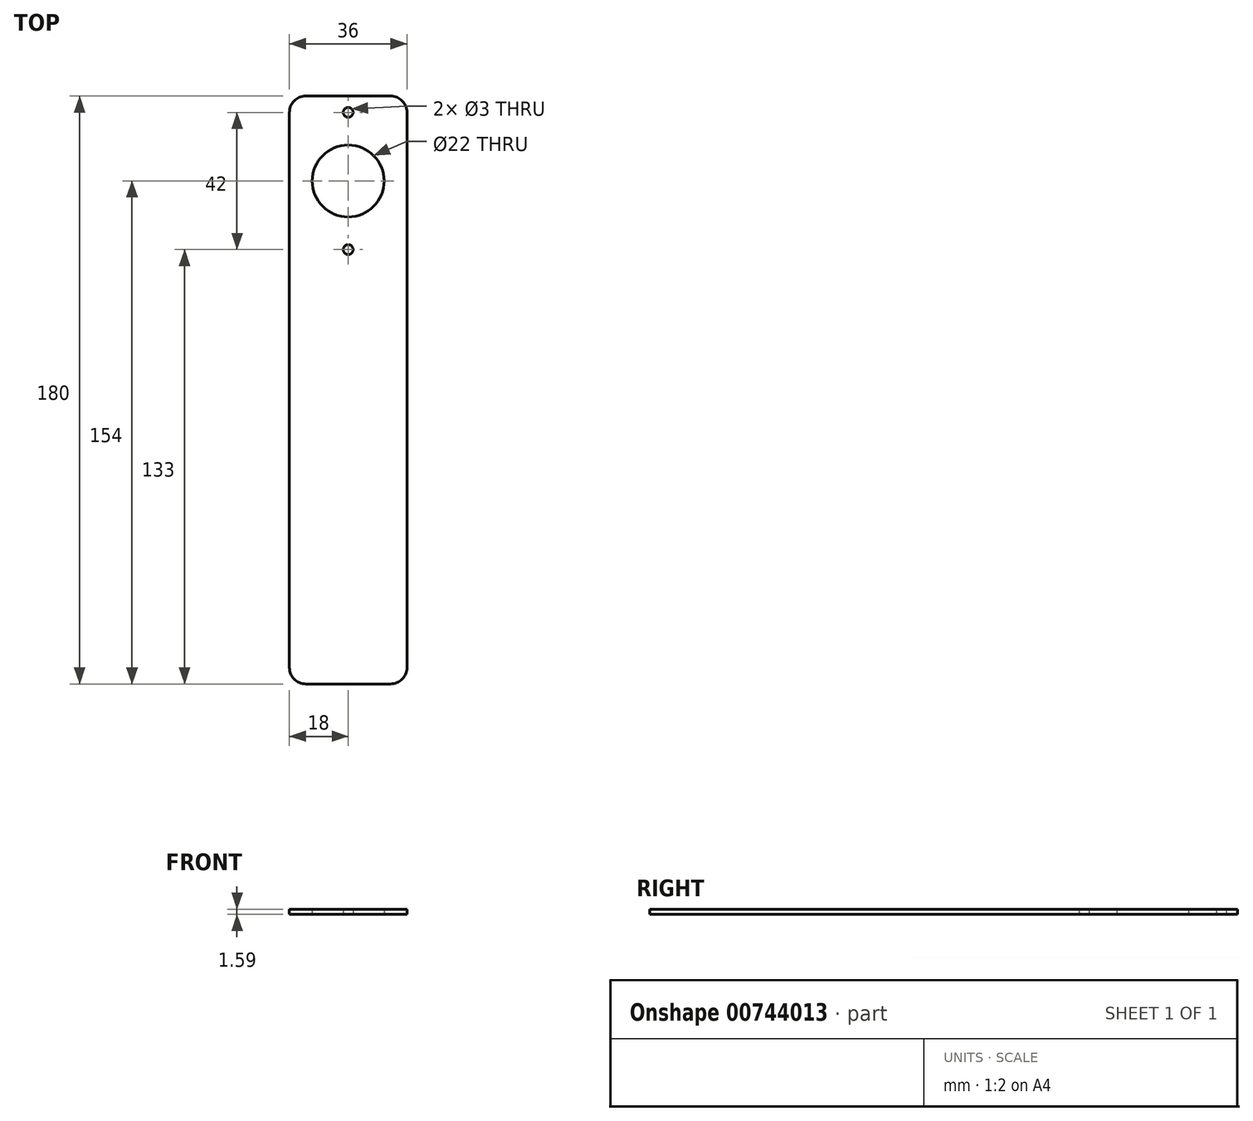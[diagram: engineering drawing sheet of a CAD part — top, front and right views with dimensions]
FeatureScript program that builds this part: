
annotation { "Feature Type Name" : "Feature", "Feature Type Description" : "" }
export const myFeature = defineFeature(function(context is Context, id is Id, definition is map)
    precondition{}
    {
        {
            var Q0;
            Q0=qCreatedBy(makeId("Top.planeOp"),FACE);
            var sketch = newSketch(context, id + "F0", { "sketchPlane" : qUnion([Q0])});
            skLineSegment(sketch, "E0.bottom", {"start": v(-13, 180) * mm, "end": v(13, 180) * mm});
            skLineSegment(sketch, "E0.top", {"start": v(-13, 0) * mm, "end": v(13, 0) * mm});
            skLineSegment(sketch, "E0.left", {"start": v(-18, 175) * mm, "end": v(-18, 5) * mm});
            skLineSegment(sketch, "E0.right", {"start": v(18, 175) * mm, "end": v(18, 5) * mm});
            skPoint(sketch, "E1.visualSharp", {"position": v(-18, 180) * mm});
            skArc(sketch, "E1.filletArc", {"start": v(-13, 180) * mm, "mid": v(-16.54, 178.54) * mm, "end": v(-18, 175) * mm});
            skPoint(sketch, "E2.visualSharp", {"position": v(18, 180) * mm});
            skArc(sketch, "E2.filletArc", {"start": v(18, 175) * mm, "mid": v(16.54, 178.54) * mm, "end": v(13, 180) * mm});
            skPoint(sketch, "E3.visualSharp", {"position": v(-18, 0) * mm});
            skArc(sketch, "E3.filletArc", {"start": v(-18, 5) * mm, "mid": v(-16.54, 1.46) * mm, "end": v(-13, 0) * mm});
            skPoint(sketch, "E4.visualSharp", {"position": v(18, 0) * mm});
            skArc(sketch, "E4.filletArc", {"start": v(13, 0) * mm, "mid": v(16.54, 1.46) * mm, "end": v(18, 5) * mm});
            skCircle(sketch, "E5", {"center": v(0, 154) * mm, "radius": 11 * mm});
            skCircle(sketch, "E6", {"center": v(0, 154) * mm, "radius": 21 * mm, "construction": true});
            skCircle(sketch, "E7", {"center": v(0, 175) * mm, "radius": 1.5 * mm});
            skCircle(sketch, "E8", {"center": v(0, 133) * mm, "radius": 1.5 * mm});
            skLineSegment(sketch, "E9", {"start": v(0, 154) * mm, "end": v(0, 180) * mm, "construction": true});
            skSolve(sketch);
        }
        {
            var Q0;
            Q0 = qSketchRegion(id + "F0", true);
            extrude(context, id + "F1", {"entities" : qUnion([Q0]), "depth" : 1.59 * mm, "offsetDistance" : 25 * mm});
        }
    });
